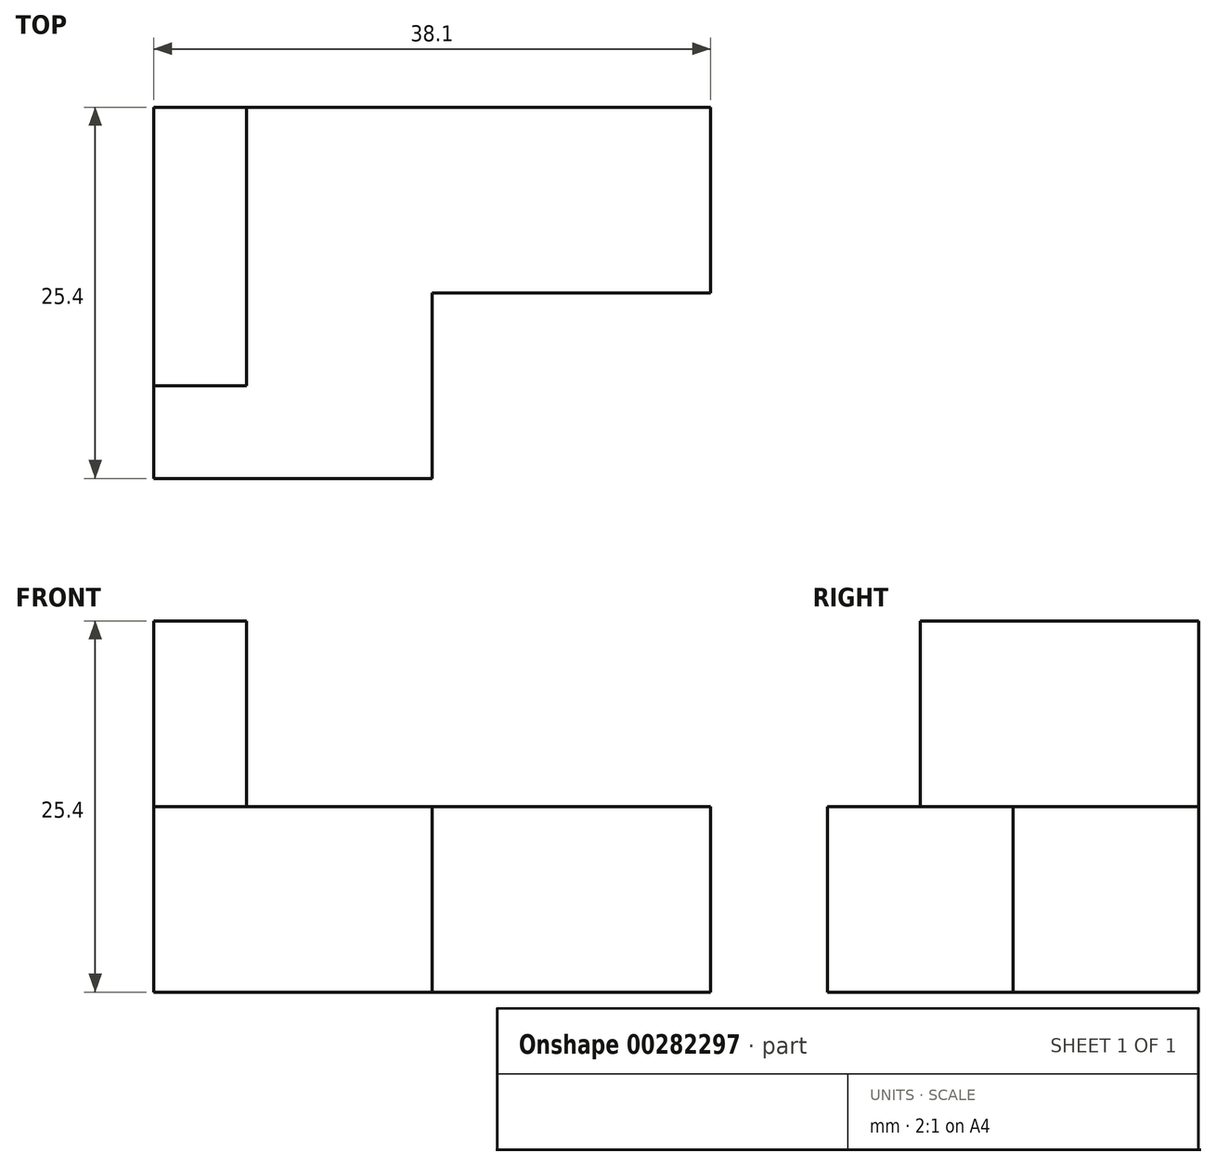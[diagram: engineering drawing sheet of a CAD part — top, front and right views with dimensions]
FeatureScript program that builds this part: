
annotation { "Feature Type Name" : "Feature", "Feature Type Description" : "" }
export const myFeature = defineFeature(function(context is Context, id is Id, definition is map)
    precondition{}
    {
        {
            var Q0;
            Q0=qCreatedBy(makeId("Front.planeOp"),FACE);
            var sketch = newSketch(context, id + "F0", { "sketchPlane" : qUnion([Q0])});
            skLineSegment(sketch, "E0", {"start": v(0, 0) * mm, "end": v(0, 12.7) * mm});
            skLineSegment(sketch, "E1", {"start": v(0, 12.7) * mm, "end": v(19.05, 12.7) * mm});
            skLineSegment(sketch, "E2", {"start": v(19.05, 12.7) * mm, "end": v(19.05, 0) * mm});
            skLineSegment(sketch, "E3", {"start": v(19.05, 0) * mm, "end": v(0, 0) * mm});
            skSolve(sketch);
        }
        {
            var Q0;
            Q0=makeQuery(id+"F0.imprint","IMPRINT",FACE,{"disambiguationData":[TD([[makeQuery(id+"F0.imprint","IMPRINT",EDGE,{"derivedFrom":sQuery(id+"F0.wireOp",EDGE,"E0")}),-1.0]])]});
            extrude(context, id + "F1", {"entities" : qUnion([Q0]), "oppositeDirection" : true, "depth" : 25.4 * mm});
        }
        {
            var Q0;
            Q0=qCreatedBy(makeId("Top.planeOp"),FACE);
            var sketch = newSketch(context, id + "F2", { "sketchPlane" : qUnion([Q0])});
            skLineSegment(sketch, "E4.bottom", {"start": v(19.05, 25.4) * mm, "end": v(38.1, 25.4) * mm});
            skLineSegment(sketch, "E4.top", {"start": v(19.05, 12.7) * mm, "end": v(38.1, 12.7) * mm});
            skLineSegment(sketch, "E4.left", {"start": v(19.05, 25.4) * mm, "end": v(19.05, 12.7) * mm});
            skLineSegment(sketch, "E4.right", {"start": v(38.1, 25.4) * mm, "end": v(38.1, 12.7) * mm});
            skSolve(sketch);
        }
        {
            var Q0;
            Q0=makeQuery(id+"F2.imprint","IMPRINT",FACE,{"disambiguationData":[TD([[makeQuery(id+"F2.imprint","IMPRINT",EDGE,{"derivedFrom":sQuery(id+"F2.wireOp",EDGE,"E4.bottom")}),-1.0]])]});
            extrude(context, id + "F3", {"entities" : qUnion([Q0]), "operationType" : NewBodyOperationType.ADD, "depth" : 12.7 * mm});
        }
        {
            var Q0;
            Q0=qCreatedBy(makeId("Top.planeOp"),FACE);
            var sketch = newSketch(context, id + "F4", { "sketchPlane" : qUnion([Q0])});
            skLineSegment(sketch, "E5", {"start": v(0, 25.4) * mm, "end": v(0, 6.35) * mm});
            skLineSegment(sketch, "E6", {"start": v(0, 6.35) * mm, "end": v(6.35, 6.35) * mm});
            skLineSegment(sketch, "E7", {"start": v(6.35, 6.35) * mm, "end": v(6.35, 25.4) * mm});
            skLineSegment(sketch, "E8", {"start": v(6.35, 25.4) * mm, "end": v(0, 25.4) * mm});
            skSolve(sketch);
        }
        {
            var Q0;
            Q0 = qSketchRegion(id + "F4", true);
            extrude(context, id + "F5", {"entities" : qUnion([Q0]), "operationType" : NewBodyOperationType.ADD, "depth" : 25.4 * mm});
        }
    });
